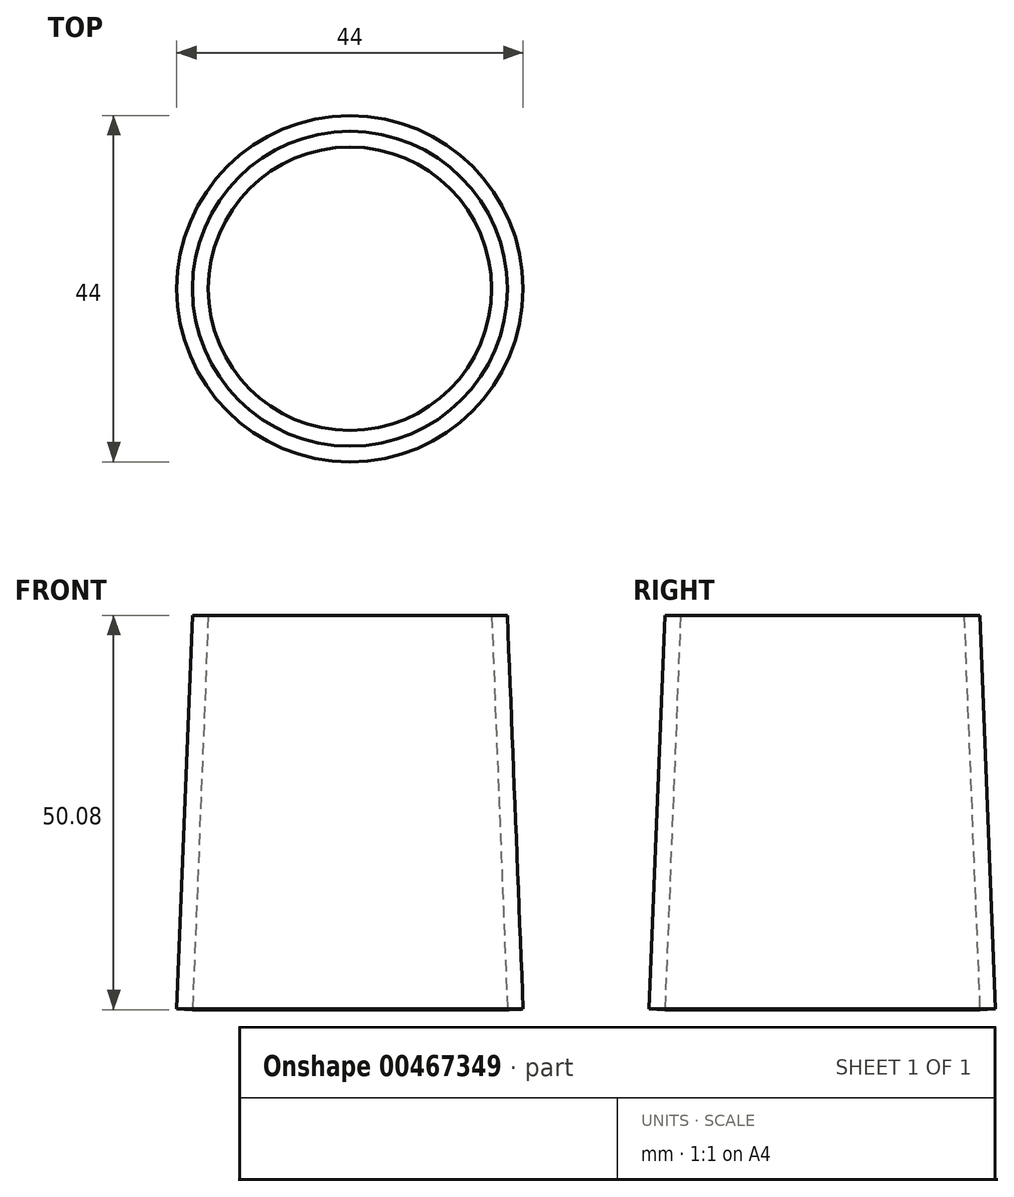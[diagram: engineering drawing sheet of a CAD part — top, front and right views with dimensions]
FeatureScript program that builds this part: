
annotation { "Feature Type Name" : "Feature", "Feature Type Description" : "" }
export const myFeature = defineFeature(function(context is Context, id is Id, definition is map)
    precondition{}
    {
        {
            var Q0;
            Q0=qCreatedBy(makeId("Right.planeOp"),FACE);
            var sketch = newSketch(context, id + "F0", { "sketchPlane" : qUnion([Q0])});
            skLineSegment(sketch, "E0", {"start": v(18, 31.12) * mm, "end": v(20, -18.88) * mm});
            skLineSegment(sketch, "E1.0", {"start": v(20, 31.2) * mm, "end": v(22, -18.8) * mm});
            skLineSegment(sketch, "E2", {"start": v(18, 31.12) * mm, "end": v(20, 31.2) * mm});
            skLineSegment(sketch, "E3", {"start": v(20, -18.88) * mm, "end": v(22, -18.8) * mm});
            skLineSegment(sketch, "E4", {"start": v(0, 41.22) * mm, "end": v(0, -25.22) * mm});
            skSolve(sketch);
        }
        {
            var Q0;
            Q0=makeQuery(id+"F0.imprint","IMPRINT",FACE,{"disambiguationData":[TD([[makeQuery(id+"F0.imprint","IMPRINT",EDGE,{"derivedFrom":sQuery(id+"F0.wireOp",EDGE,"E0")}),1.0]])]});
            var Q1;
            Q1=sQuery(id+"F0.wireOp",EDGE,"E4");
            revolve(context, id + "F1", {"entities" : qUnion([Q0]), "axis" : qUnion([Q1]), "revolveType" : RevolveType.FULL});
        }
    });
